# Revit family: 8174060xx--Sanitary_Bathroom-Accessories_Roca_8174060xx-Public-Wall-mounted-industrial-paper-dispenser
name_source: partatom
category: Furniture
units: mm (PartAtom-declared; Revit-internal decimal feet)

## family parameters
Always vertical = No
Cut with Voids When Loaded = No
OmniClass Number = 23.21.43.15.29
Room Calculation Point = No
Shared = No
Work Plane-Based = No

## types (2) — shared parameters
BIMobject category = Bathroom Accessories
BIMobject category code = sanitary-accessories1
BIMobject main category = Sanitary
BIMobject main category code = sanitary
Brand url = http://www.roca.com
Description = Wall-mounted industrial paper dispenser. Designed to be used in highly transited areas such as hospitals, shopping centers, hotels or academic centers, Roca’s range of accessories for public spaces combines resistance, safety and functionality in a wide range of proposals. Specifically conceived for an intensive use, all products within the Public collection are manufactured with highly durable materials, designed to facilitate the work of maintenance and cleaning personnel.
Design country = Spain
Edition number = 1
IFC Classification = Furnishing Element
Manufacturer = Roca
Manufacturer country = Spain
Manufacturer name = Roca
Masterformat 2014 Code = 10 28 13
Masterformat 2014 Description = Toilet Accessories
Material main = Stainless steel
Model = 8174060xx Public Wall-mounted industrial paper dispenser
OmniClass Code = 23-21 43 15 29
OmniClass Description = Toilet Accessories Dispensers
Product Guid = fc5fad11-53f9-4323-a7e5-c1ae1f9b6c96
Product SKU = 8174060xx
Product data url = https://bimobject.com
Product family = Accessories
Product group = Public
Product name = 8174060xx Public Wall-mounted industrial paper dispenser
Product url = https://www.export.roca.com
QR code = https://www.roca.com
Technical description = http://www.export.roca.com
URL = http://www.roca.com
Uniclass 2015 Code = Pr_40_70_22_90
Uniclass 2015 Name = Toilet paper dispensers
Uniformat II Code = E2010
Uniformat II Description = Fixed Furnishings
Youtube clip = https://www.youtube.com

## per-type parameters (varying)
| type | Main Material |
| 01 - Polished | Roca - PUBLIC - 01 Polished |
| 02 - Matt | Roca - PUBLIC - 02 Matt |

## geometry (parser evidence)
native form markers: Blend x2, Sweep x4
no freeform markers — native parametric forms only
